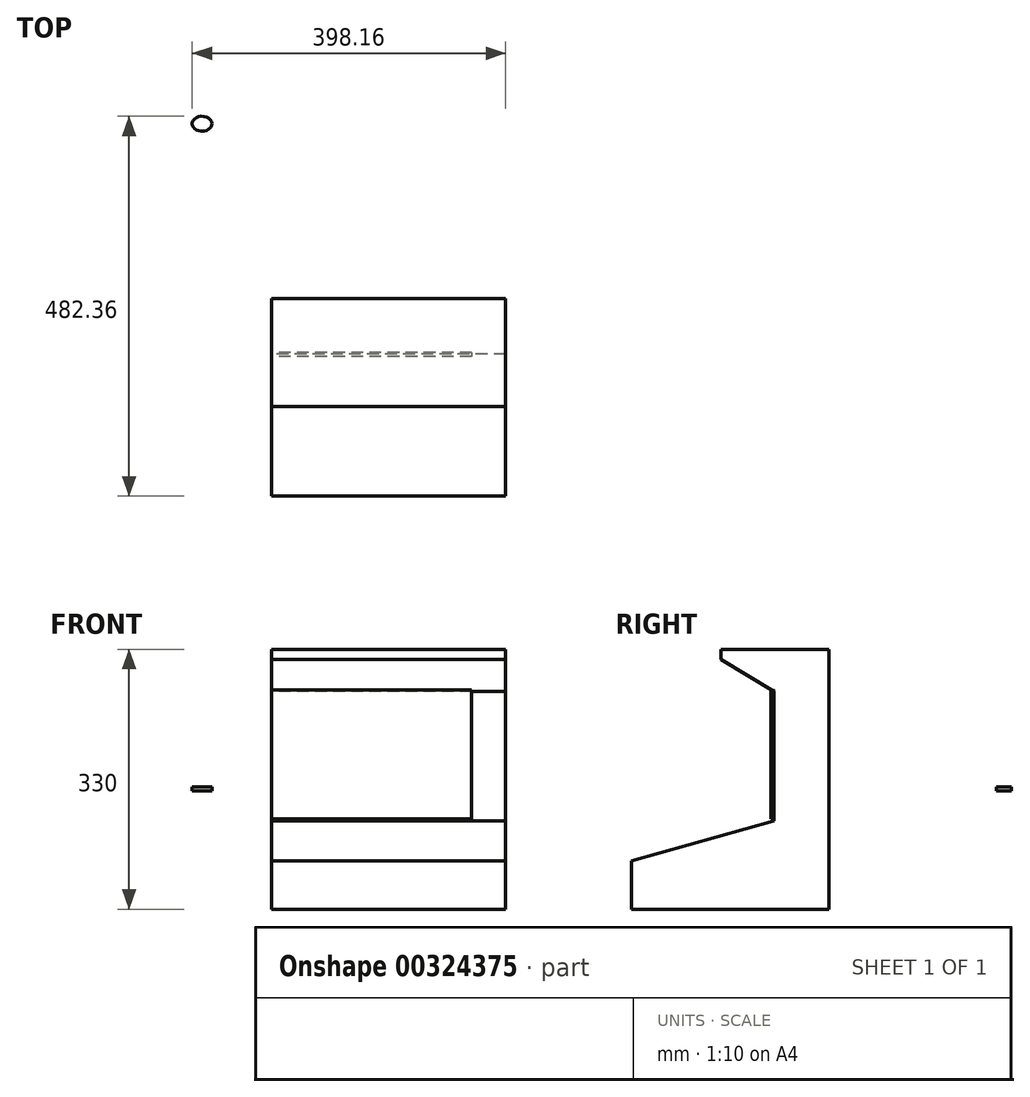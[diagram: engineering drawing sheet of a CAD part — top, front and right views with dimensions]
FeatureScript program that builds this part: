
annotation { "Feature Type Name" : "Feature", "Feature Type Description" : "" }
export const myFeature = defineFeature(function(context is Context, id is Id, definition is map)
    precondition{}
    {
        {
            var Q0;
            Q0=qCreatedBy(makeId("Right.planeOp"),FACE);
            var sketch = newSketch(context, id + "F0", { "sketchPlane" : qUnion([Q0])});
            skLineSegment(sketch, "E0", {"start": v(59.72, -150.27) * mm, "end": v(59.72, 179.73) * mm});
            skLineSegment(sketch, "E1", {"start": v(59.72, -150.27) * mm, "end": v(-191.1, -150.27) * mm});
            skLineSegment(sketch, "E2", {"start": v(-191.1, -150.27) * mm, "end": v(-191.1, -88.94) * mm});
            skLineSegment(sketch, "E3", {"start": v(-191.1, -88.94) * mm, "end": v(-10.5, -37.79) * mm});
            skLineSegment(sketch, "E4", {"start": v(-10.5, -37.79) * mm, "end": v(-10.5, 126.4) * mm});
            skLineSegment(sketch, "E5", {"start": v(-10.5, 126.4) * mm, "end": v(-77.43, 166.81) * mm});
            skLineSegment(sketch, "E6", {"start": v(59.72, 179.73) * mm, "end": v(-77.43, 179.73) * mm});
            skLineSegment(sketch, "E7", {"start": v(-77.43, 179.73) * mm, "end": v(-77.43, 166.81) * mm});
            skSolve(sketch);
        }
        {
            var Q0;
            Q0=makeQuery(id+"F0.imprint","IMPRINT",FACE,{"disambiguationData":[TD([[makeQuery(id+"F0.imprint","IMPRINT",EDGE,{"derivedFrom":sQuery(id+"F0.wireOp",EDGE,"E0")}),1.0]])]});
            extrude(context, id + "F1", {"entities" : qUnion([Q0]), "depth" : 297 * mm});
        }
        {
            var Q0;
            Q0=qCreatedBy(makeId("Right.planeOp"),FACE);
            var sketch = newSketch(context, id + "F2", { "sketchPlane" : qUnion([Q0])});
            skLineSegment(sketch, "E8.bottom", {"start": v(-8.9, -35.6) * mm, "end": v(-13.94, -35.6) * mm});
            skLineSegment(sketch, "E8.top", {"start": v(-8.9, 128.47) * mm, "end": v(-13.94, 128.47) * mm});
            skLineSegment(sketch, "E8.left", {"start": v(-8.9, -35.6) * mm, "end": v(-8.9, 128.47) * mm});
            skLineSegment(sketch, "E8.right", {"start": v(-13.94, -35.6) * mm, "end": v(-13.94, 128.47) * mm});
            skSolve(sketch);
        }
        {
            var Q0;
            Q0 = qSketchRegion(id + "F2", true);
            extrude(context, id + "F3", {"entities" : qUnion([Q0]), "depth" : 254 * mm});
        }
        {
            var Q0;
            Q0=qCreatedBy(makeId("Top.planeOp"),FACE);
            var sketch = newSketch(context, id + "F4", { "sketchPlane" : qUnion([Q0])});
            skEllipse(sketch, "E9", {"center": v(-238.66, 281.76) * mm, "majorRadius": 12.5 * mm, "minorRadius": 9.5 * mm, "majorAxis": v(1, 0)});
            skSolve(sketch);
        }
        {
            var Q0;
            Q0=makeQuery(id+"F4.imprint","IMPRINT",FACE,{"disambiguationData":[TD([[makeQuery(id+"F4.imprint","IMPRINT",EDGE,{"derivedFrom":sQuery(id+"F4.wireOp",EDGE,"E9")}),1.0]])]});
            extrude(context, id + "F5", {"entities" : qUnion([Q0]), "depth" : 5 * mm});
        }
        {
            var Q0;
            Q0=makeQuery(id+"F1.opExtrude","CAP_EDGE",EDGE,{"disambiguationData":[OSD([sQuery(id+"F0.wireOp",EDGE,"E3")])],"isStart":true});
            cPoint(context, id + "F6", {"entities" : qUnion([Q0]), "parameter" : 0.5});
        }
        {
            var Q0;
            Q0=makeQuery(id+"F5.opExtrude","SWEPT_BODY",BODY,{"disambiguationData":[OSD([sQuery(id+"F4.wireOp",EDGE,"E9")])]});
            var Q1;
            Q1 = qCreatedBy(id + "F6" ,VERTEX);
            var Q2;
            Q2=qCreatedBy(makeId("Right.planeOp"),FACE);
            transform(context, id + "F7", {"entities" : qUnion([Q0]), "transformType" : TransformType.TRANSLATION_DISTANCE, "transformDirection" : qUnion([Q2]), "distance" : 150 * mm, "makeCopy" : false});
        }
    });
